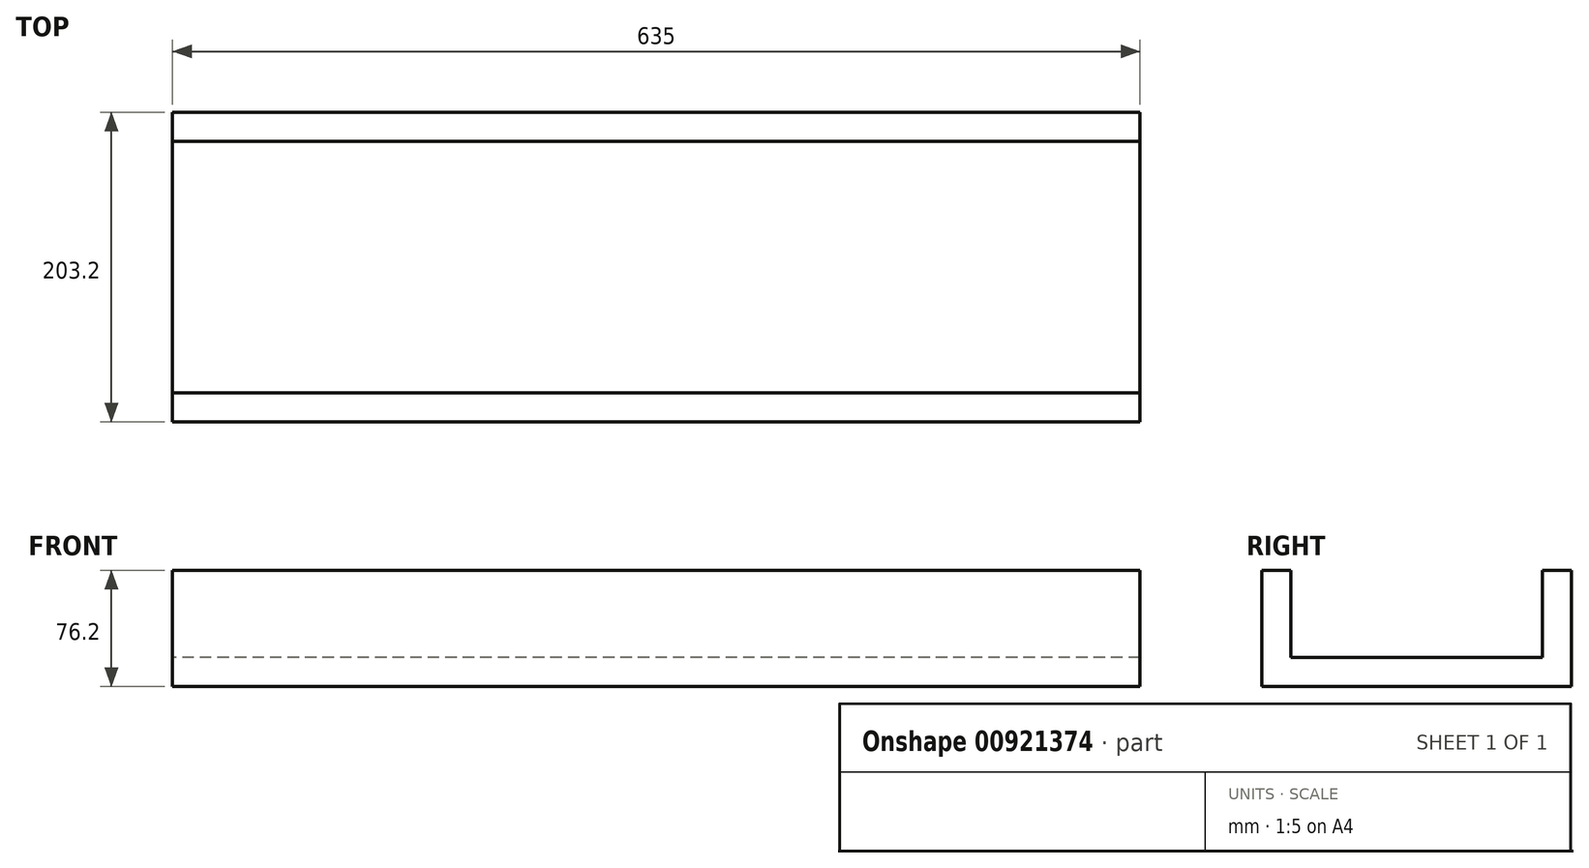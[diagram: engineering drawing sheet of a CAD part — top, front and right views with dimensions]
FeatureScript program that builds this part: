
annotation { "Feature Type Name" : "Feature", "Feature Type Description" : "" }
export const myFeature = defineFeature(function(context is Context, id is Id, definition is map)
    precondition{}
    {
        {
            var Q0;
            Q0=qCreatedBy(makeId("Right.planeOp"),FACE);
            var sketch = newSketch(context, id + "F0", { "sketchPlane" : qUnion([Q0])});
            skLineSegment(sketch, "E0.bottom", {"start": v(-101.6, 38.1) * mm, "end": v(-82.55, 38.1) * mm});
            skLineSegment(sketch, "E0.top", {"start": v(-101.6, -38.1) * mm, "end": v(101.6, -38.1) * mm});
            skLineSegment(sketch, "E0.left", {"start": v(-101.6, 38.1) * mm, "end": v(-101.6, -38.1) * mm});
            skLineSegment(sketch, "E0.right", {"start": v(101.6, 38.1) * mm, "end": v(101.6, -38.1) * mm});
            skLineSegment(sketch, "E1", {"start": v(-101.6, 38.1) * mm, "end": v(101.6, -38.1) * mm, "construction": true});
            skLineSegment(sketch, "E2.top", {"start": v(-82.55, -19.05) * mm, "end": v(82.55, -19.05) * mm});
            skLineSegment(sketch, "E2.left", {"start": v(-82.55, 38.1) * mm, "end": v(-82.55, -19.05) * mm});
            skLineSegment(sketch, "E2.right", {"start": v(82.55, 38.1) * mm, "end": v(82.55, -19.05) * mm});
            skLineSegment(sketch, "E3.trimOffspring", {"start": v(82.55, 38.1) * mm, "end": v(101.6, 38.1) * mm});
            skSolve(sketch);
        }
        {
            var Q0;
            Q0 = qSketchRegion(id + "F0", true);
            extrude(context, id + "F1", {"entities" : qUnion([Q0]), "endBound" : BoundingType.SYMMETRIC, "depth" : 635 * mm, "offsetDistance" : 25.4 * mm});
        }
    });
